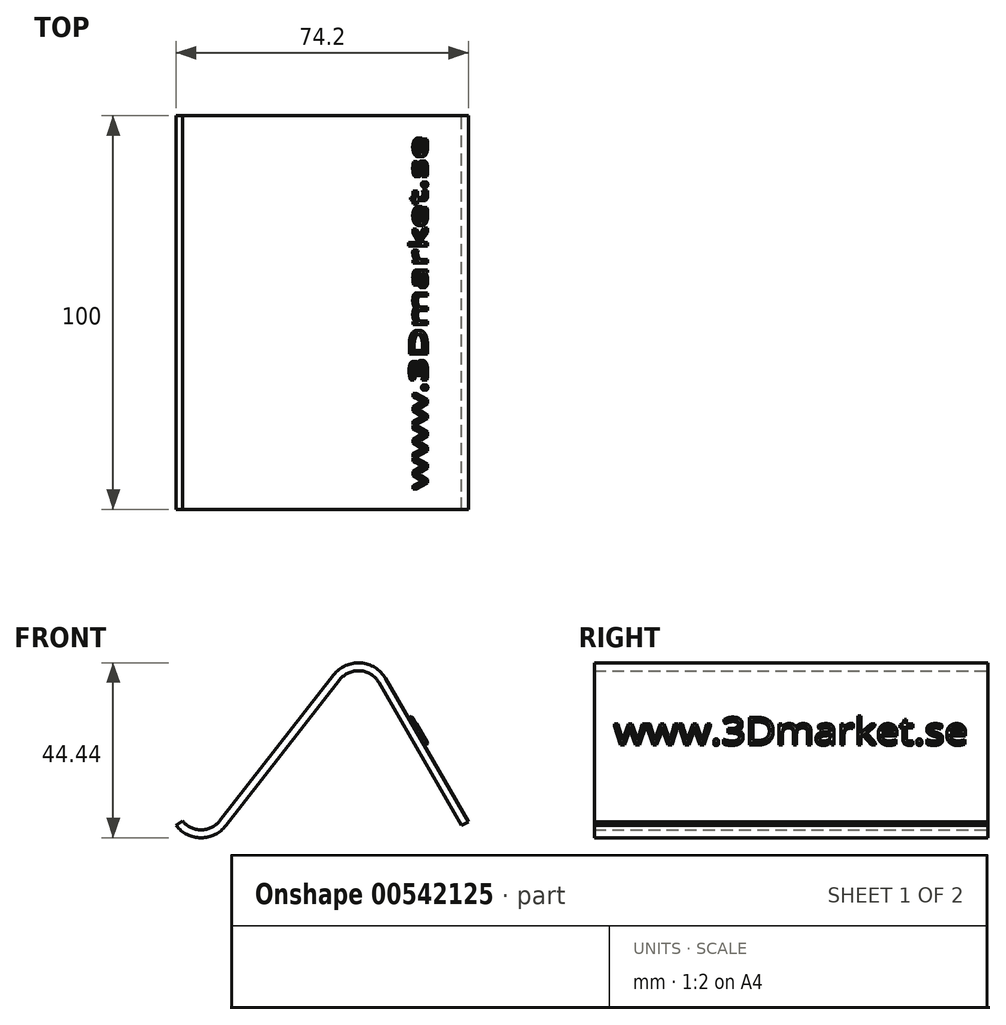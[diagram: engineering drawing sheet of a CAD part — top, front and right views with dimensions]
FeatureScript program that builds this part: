
annotation { "Feature Type Name" : "Feature", "Feature Type Description" : "" }
export const myFeature = defineFeature(function(context is Context, id is Id, definition is map)
    precondition{}
    {
        {
            var Q0;
            Q0=qCreatedBy(makeId("Front.planeOp"),FACE);
            var sketch = newSketch(context, id + "F0", { "sketchPlane" : qUnion([Q0])});
            skLineSegment(sketch, "E0", {"start": v(-33.65, 0) * mm, "end": v(-4.73, 37.05) * mm});
            skLineSegment(sketch, "E1", {"start": v(5.2, 36.36) * mm, "end": v(26.21, 0) * mm});
            skArc(sketch, "E2.filletArc", {"start": v(5.2, 36.36) * mm, "mid": v(0.42, 39.35) * mm, "end": v(-4.73, 37.05) * mm});
            skArc(sketch, "E3", {"start": v(-33.65, 0) * mm, "mid": v(-39.95, -3.08) * mm, "end": v(-46.26, 0) * mm});
            skLineSegment(sketch, "E4.0", {"start": v(6.93, 37.36) * mm, "end": v(27.94, 1) * mm});
            skArc(sketch, "E4.1", {"start": v(6.93, 37.36) * mm, "mid": v(0.55, 41.34) * mm, "end": v(-6.3, 38.28) * mm});
            skLineSegment(sketch, "E4.2", {"start": v(-35.22, 1.23) * mm, "end": v(-6.3, 38.28) * mm});
            skArc(sketch, "E4.3", {"start": v(-35.22, 1.23) * mm, "mid": v(-39.95, -1.08) * mm, "end": v(-44.68, 1.23) * mm});
            skLineSegment(sketch, "E5", {"start": v(-46.26, 0) * mm, "end": v(-44.68, 1.23) * mm});
            skLineSegment(sketch, "E6", {"start": v(26.21, 0) * mm, "end": v(27.94, 1) * mm});
            skSolve(sketch);
        }
        {
            var Q0;
            Q0=makeQuery(id+"F0.imprint","IMPRINT",FACE,{"disambiguationData":[TD([[makeQuery(id+"F0.imprint","IMPRINT",EDGE,{"derivedFrom":sQuery(id+"F0.wireOp",EDGE,"E0")}),1.0]])]});
            extrude(context, id + "F1", {"entities" : qUnion([Q0]), "depth" : 100 * mm, "offsetDistance" : 25 * mm});
        }
        {
            var Q0;
            Q0=makeQuery(id+"F1.opExtrude","SWEPT_FACE",FACE,{"disambiguationData":[OSD([sQuery(id+"F0.wireOp",EDGE,"E4.0")])]});
            var sketch = newSketch(context, id + "F2", { "sketchPlane" : qUnion([Q0])});
            skText(sketch, "E7", { "text": "www.3Dmarket.se\n", "fontName": "OpenSans-Regular.ttf"});
            const initialGuessF2  = {"E7": [-0.095, 0.00937, 1, 0, 0.00758]};
            skSetInitialGuess(sketch, initialGuessF2);
            skSolve(sketch);
        }
        {
            var Q0;
            Q0 = qSketchRegion(id + "F2", true);
            extrude(context, id + "F3", {"entities" : qUnion([Q0]), "operationType" : NewBodyOperationType.ADD, "depth" : 1 * mm, "offsetDistance" : 25 * mm});
        }
    });
